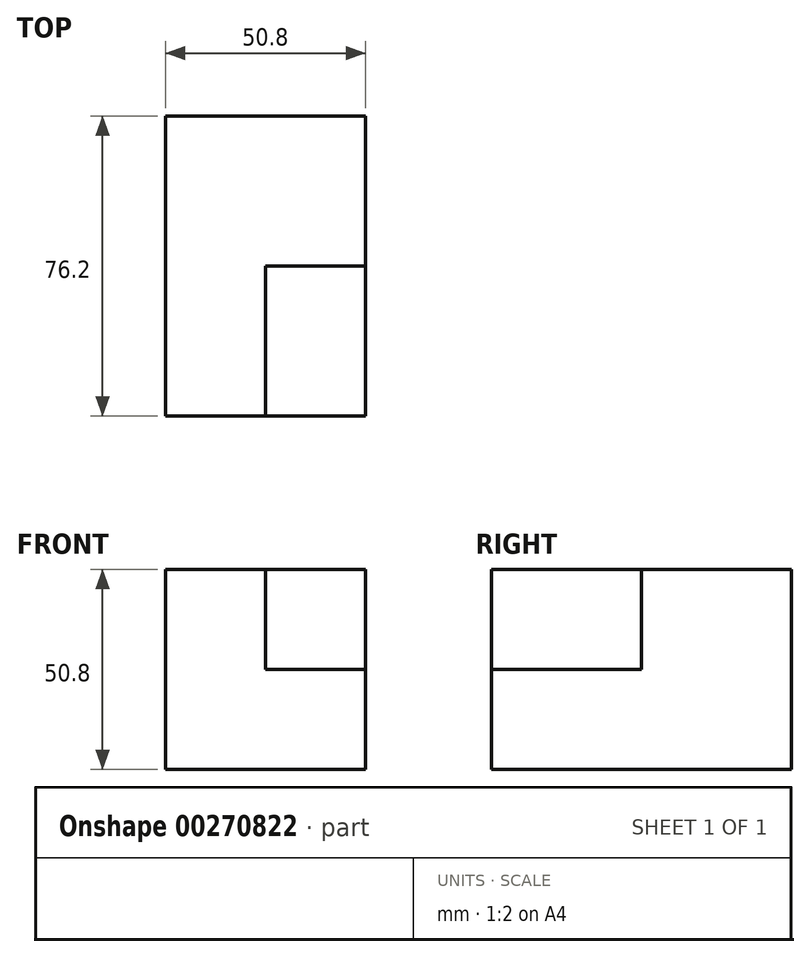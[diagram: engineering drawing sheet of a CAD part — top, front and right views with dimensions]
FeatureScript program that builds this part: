
annotation { "Feature Type Name" : "Feature", "Feature Type Description" : "" }
export const myFeature = defineFeature(function(context is Context, id is Id, definition is map)
    precondition{}
    {
        {
            var Q0;
            Q0=qCreatedBy(makeId("Front.planeOp"),FACE);
            var sketch = newSketch(context, id + "F0", { "sketchPlane" : qUnion([Q0])});
            skLineSegment(sketch, "E0.bottom", {"start": v(0, 0) * mm, "end": v(-50.8, 0) * mm});
            skLineSegment(sketch, "E0.top", {"start": v(0, 50.8) * mm, "end": v(-50.8, 50.8) * mm});
            skLineSegment(sketch, "E0.left", {"start": v(0, 0) * mm, "end": v(0, 50.8) * mm});
            skLineSegment(sketch, "E0.right", {"start": v(-50.8, 0) * mm, "end": v(-50.8, 50.8) * mm});
            skLineSegment(sketch, "E1.bottom", {"start": v(0, 50.8) * mm, "end": v(-25.4, 50.8) * mm});
            skLineSegment(sketch, "E1.top", {"start": v(0, 25.4) * mm, "end": v(-25.4, 25.4) * mm});
            skLineSegment(sketch, "E1.left", {"start": v(0, 50.8) * mm, "end": v(0, 25.4) * mm});
            skLineSegment(sketch, "E1.right", {"start": v(-25.4, 50.8) * mm, "end": v(-25.4, 25.4) * mm});
            skSolve(sketch);
        }
        {
            var Q0;
            Q0 = qSketchRegion(id + "F0", true);
            extrude(context, id + "F1", {"entities" : qUnion([Q0]), "depth" : 76.2 * mm});
        }
        {
            var Q0;
            Q0=makeQuery(id+"F1.opExtrude","CAP_FACE",FACE,{"disambiguationData":[OSD([sQuery(id+"F0.wireOp",EDGE,"E0.bottom"),sQuery(id+"F0.wireOp",EDGE,"E0.top"),sQuery(id+"F0.wireOp",EDGE,"E0.left"),sQuery(id+"F0.wireOp",EDGE,"E0.right"),sQuery(id+"F0.wireOp",EDGE,"E1.bottom"),sQuery(id+"F0.wireOp",EDGE,"E1.left")])],"isStart":false});
            var sketch = newSketch(context, id + "F2", { "sketchPlane" : qUnion([Q0])});
            skLineSegment(sketch, "E2.bottom", {"start": v(0, 50.8) * mm, "end": v(-25.4, 50.8) * mm});
            skLineSegment(sketch, "E2.top", {"start": v(0, 25.4) * mm, "end": v(-25.4, 25.4) * mm});
            skLineSegment(sketch, "E2.left", {"start": v(0, 50.8) * mm, "end": v(0, 25.4) * mm});
            skLineSegment(sketch, "E2.right", {"start": v(-25.4, 50.8) * mm, "end": v(-25.4, 25.4) * mm});
            skSolve(sketch);
        }
        {
            var Q0;
            Q0 = qSketchRegion(id + "F2", true);
            extrude(context, id + "F3", {"entities" : qUnion([Q0]), "operationType" : NewBodyOperationType.REMOVE, "oppositeDirection" : true, "depth" : 38.1 * mm});
        }
    });
